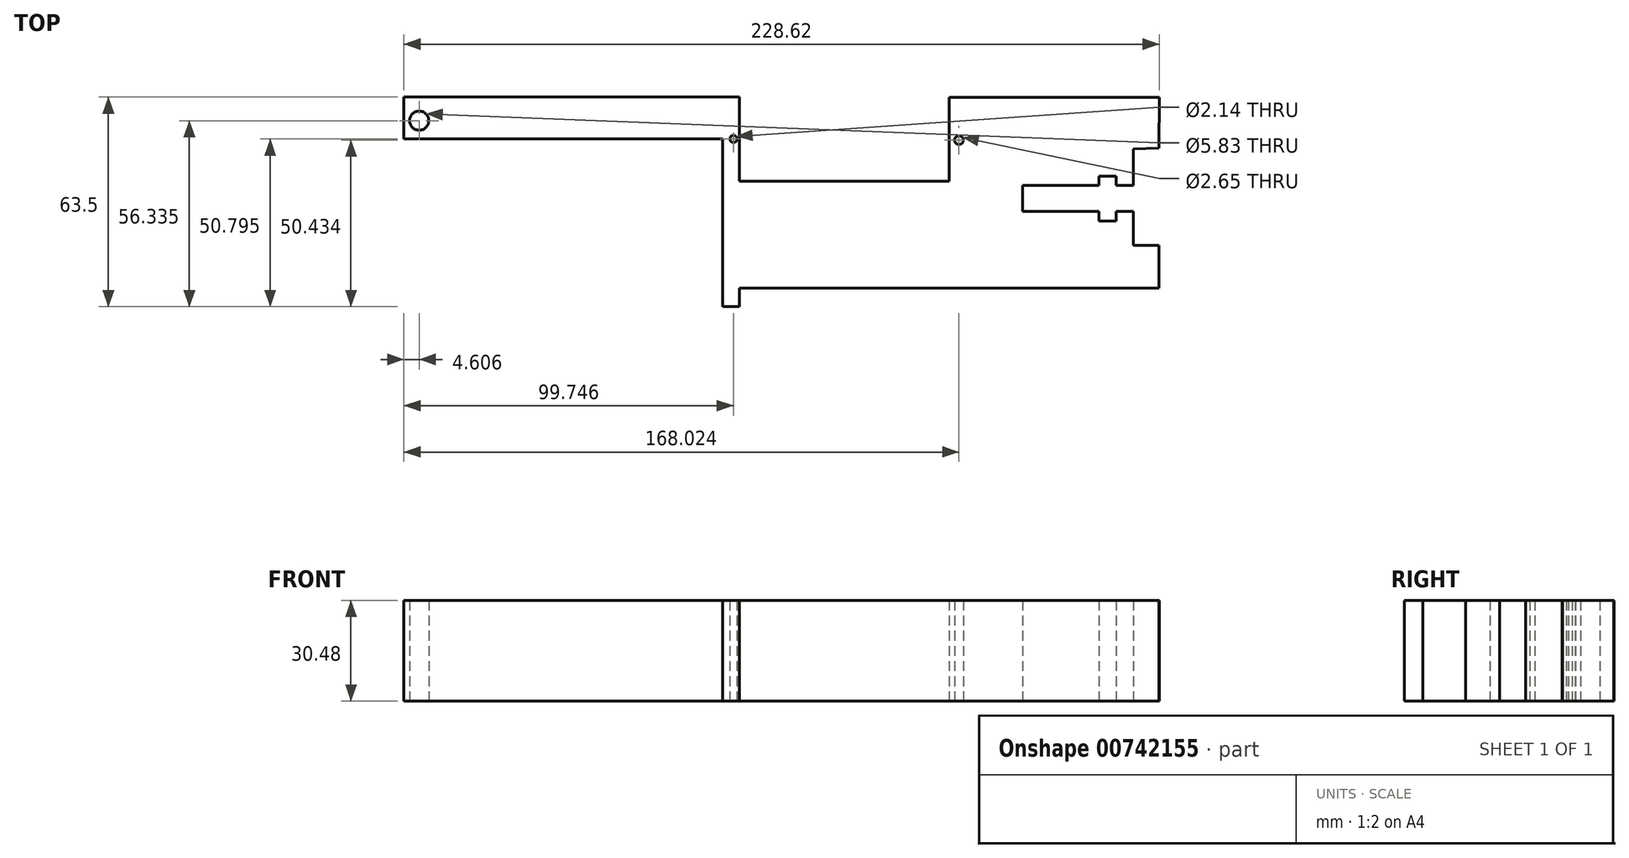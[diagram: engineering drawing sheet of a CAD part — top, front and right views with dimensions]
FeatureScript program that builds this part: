
annotation { "Feature Type Name" : "Feature", "Feature Type Description" : "" }
export const myFeature = defineFeature(function(context is Context, id is Id, definition is map)
    precondition{}
    {
        {
            var Q0;
            Q0=qCreatedBy(makeId("Top.planeOp"),FACE);
            var sketch = newSketch(context, id + "F0", { "sketchPlane" : qUnion([Q0])});
            skLineSegment(sketch, "E0.bottom", {"start": v(-95.7, 37.6) * mm, "end": v(5.9, 37.6) * mm});
            skLineSegment(sketch, "E0.top", {"start": v(-95.7, 24.9) * mm, "end": v(5.9, 24.9) * mm});
            skLineSegment(sketch, "E0.left", {"start": v(-95.7, 37.6) * mm, "end": v(-95.7, 24.9) * mm});
            skLineSegment(sketch, "E0.right", {"start": v(5.9, 37.6) * mm, "end": v(5.9, 24.9) * mm});
            skLineSegment(sketch, "E1.bottom", {"start": v(5.9, 37.6) * mm, "end": v(0.82, 37.6) * mm});
            skLineSegment(sketch, "E1.top", {"start": v(5.9, -25.9) * mm, "end": v(0.82, -25.9) * mm});
            skLineSegment(sketch, "E1.left", {"start": v(5.9, 37.6) * mm, "end": v(5.9, -25.9) * mm});
            skLineSegment(sketch, "E1.right", {"start": v(0.82, 37.6) * mm, "end": v(0.82, -25.9) * mm});
            skLineSegment(sketch, "E2", {"start": v(5.9, -25.9) * mm, "end": v(5.9, -20.3) * mm});
            skLineSegment(sketch, "E3", {"start": v(5.9, -20.3) * mm, "end": v(132.9, -20.3) * mm});
            skLineSegment(sketch, "E4", {"start": v(5.9, 37.6) * mm, "end": v(5.9, 12.14) * mm});
            skLineSegment(sketch, "E5", {"start": v(5.9, 12.14) * mm, "end": v(132.9, 12.14) * mm});
            skLineSegment(sketch, "E6", {"start": v(132.9, 12.14) * mm, "end": v(132.9, -20.3) * mm});
            skLineSegment(sketch, "E7", {"start": v(5.9, 12.14) * mm, "end": v(69.4, 12.14) * mm});
            skLineSegment(sketch, "E8", {"start": v(69.4, 12.14) * mm, "end": v(69.4, 37.47) * mm});
            skLineSegment(sketch, "E9", {"start": v(69.4, 37.47) * mm, "end": v(132.92, 37.47) * mm});
            skLineSegment(sketch, "E10", {"start": v(132.92, 37.47) * mm, "end": v(132.9, 12.14) * mm});
            skLineSegment(sketch, "E11", {"start": v(132.92, 37.47) * mm, "end": v(132.91, 22.06) * mm});
            skLineSegment(sketch, "E12", {"start": v(132.9, -20.3) * mm, "end": v(132.9, -7.37) * mm});
            skLineSegment(sketch, "E13", {"start": v(132.9, -7.37) * mm, "end": v(125.05, -7.37) * mm});
            skLineSegment(sketch, "E14", {"start": v(125.05, -7.37) * mm, "end": v(125.05, 21.9) * mm});
            skLineSegment(sketch, "E15", {"start": v(125.05, 21.9) * mm, "end": v(132.91, 22.06) * mm});
            skLineSegment(sketch, "E16", {"start": v(125.05, -7.37) * mm, "end": v(125.05, 2.9) * mm});
            skLineSegment(sketch, "E17", {"start": v(125.05, 21.9) * mm, "end": v(125.05, 10.77) * mm});
            skLineSegment(sketch, "E18", {"start": v(125.05, 2.9) * mm, "end": v(91.6, 2.9) * mm});
            skLineSegment(sketch, "E19", {"start": v(125.05, 10.77) * mm, "end": v(91.6, 10.77) * mm});
            skLineSegment(sketch, "E20", {"start": v(91.6, 10.77) * mm, "end": v(91.6, 2.9) * mm});
            skLineSegment(sketch, "E21", {"start": v(125.05, 10.77) * mm, "end": v(119.88, 10.77) * mm});
            skLineSegment(sketch, "E22", {"start": v(125.05, 2.9) * mm, "end": v(119.88, 2.9) * mm});
            skLineSegment(sketch, "E23", {"start": v(119.88, 2.9) * mm, "end": v(119.88, 0) * mm});
            skLineSegment(sketch, "E24", {"start": v(119.88, 10.77) * mm, "end": v(119.88, 13.68) * mm});
            skLineSegment(sketch, "E25", {"start": v(119.88, 0) * mm, "end": v(114.66, 0) * mm});
            skLineSegment(sketch, "E26", {"start": v(114.66, 0) * mm, "end": v(114.66, 2.9) * mm});
            skLineSegment(sketch, "E27", {"start": v(114.66, 2.9) * mm, "end": v(119.88, 2.9) * mm});
            skLineSegment(sketch, "E28", {"start": v(119.88, 13.68) * mm, "end": v(114.66, 13.68) * mm});
            skLineSegment(sketch, "E29", {"start": v(114.66, 13.68) * mm, "end": v(114.66, 10.77) * mm});
            skLineSegment(sketch, "E30", {"start": v(114.66, 10.77) * mm, "end": v(119.88, 10.77) * mm});
            skPoint(sketch, "E31.centerSnap0", {"position": v(132.91, 24.8) * mm});
            skCircle(sketch, "E32", {"center": v(4.05, 24.9) * mm, "radius": 1.07 * mm});
            skCircle(sketch, "E33", {"center": v(72.32, 24.53) * mm, "radius": 1.33 * mm});
            skCircle(sketch, "E34", {"center": v(-91.1, 30.44) * mm, "radius": 2.91 * mm});
            skSolve(sketch);
        }
        {
            var Q0;
            {var subQ5=sQuery(id+"F0.wireOp",EDGE,"E0.left");Q0=makeQuery(id+"F0.imprint","IMPRINT",FACE,{"disambiguationData":[TD([[makeQuery(id+"F0.imprint","IMPRINT",EDGE,{"derivedFrom":subQ5}),1.0]])]});}
            var Q1;
            {var subQ0=sQuery(id+"F0.wireOp",EDGE,"E0.right");Q1=makeQuery(id+"F0.imprint","IMPRINT",FACE,{"disambiguationData":[TD([[makeQuery(id+"F0.imprint","IMPRINT",EDGE,{"derivedFrom":subQ0}),-1.0]])]});}
            var Q2;
            {var subQ7=sQuery(id+"F0.wireOp",EDGE,"E1.top");Q2=makeQuery(id+"F0.imprint","IMPRINT",FACE,{"disambiguationData":[TD([[makeQuery(id+"F0.imprint","IMPRINT",EDGE,{"derivedFrom":subQ7}),-1.0]])]});}
            var Q3;
            {var subQ12=sQuery(id+"F0.wireOp",EDGE,"E3");Q3=makeQuery(id+"F0.imprint","IMPRINT",FACE,{"disambiguationData":[TD([[makeQuery(id+"F0.imprint","IMPRINT",EDGE,{"derivedFrom":subQ12}),1.0]])]});}
            var Q4;
            {var subQ9=sQuery(id+"F0.wireOp",EDGE,"E8");Q4=makeQuery(id+"F0.imprint","IMPRINT",FACE,{"disambiguationData":[TD([[makeQuery(id+"F0.imprint","IMPRINT",EDGE,{"derivedFrom":subQ9}),-1.0]])]});}
            var Q5;
            {var subQ0=sQuery(id+"F0.wireOp",EDGE,"E14");var subQ1=sQuery(id+"F0.wireOp",EDGE,"E5");var subQ2=makeQuery(id+"F0.imprint","INTERSECT",VERTEX,{"derivedFrom":[subQ1,subQ0]});Q5=makeQuery(id+"F0.imprint","IMPRINT",FACE,{"disambiguationData":[TD([[makeQuery(id+"F0.imprint","IMPRINT",EDGE,{"disambiguationData":[TD([[subQ2,1.0]])],"derivedFrom":subQ1}),-1.0]])]});}
            extrude(context, id + "F1", {"entities" : qUnion([Q0, Q1, Q2, Q3, Q4, Q5]), "depth" : 5.08 * mm, "offsetDistance" : 25.4 * mm});
        }
        {
            var Q0;
            Q0=makeQuery(id+"F1.opExtrude","CAP_FACE",FACE,{"disambiguationData":[OSD([sQuery(id+"F0.wireOp",EDGE,"E0.bottom"),sQuery(id+"F0.wireOp",EDGE,"E0.top"),sQuery(id+"F0.wireOp",EDGE,"E0.left"),sQuery(id+"F0.wireOp",EDGE,"E0.right"),sQuery(id+"F0.wireOp",EDGE,"E1.top"),sQuery(id+"F0.wireOp",EDGE,"E1.left"),sQuery(id+"F0.wireOp",EDGE,"E1.right"),sQuery(id+"F0.wireOp",EDGE,"E3"),sQuery(id+"F0.wireOp",EDGE,"E5"),sQuery(id+"F0.wireOp",EDGE,"E6"),sQuery(id+"F0.wireOp",EDGE,"E8"),sQuery(id+"F0.wireOp",EDGE,"E9"),sQuery(id+"F0.wireOp",EDGE,"E10"),sQuery(id+"F0.wireOp",EDGE,"E13"),sQuery(id+"F0.wireOp",EDGE,"E14"),sQuery(id+"F0.wireOp",EDGE,"E15"),sQuery(id+"F0.wireOp",EDGE,"E18"),sQuery(id+"F0.wireOp",EDGE,"E19"),sQuery(id+"F0.wireOp",EDGE,"E20"),sQuery(id+"F0.wireOp",EDGE,"E23"),sQuery(id+"F0.wireOp",EDGE,"E24"),sQuery(id+"F0.wireOp",EDGE,"E25"),sQuery(id+"F0.wireOp",EDGE,"E26"),sQuery(id+"F0.wireOp",EDGE,"E28"),sQuery(id+"F0.wireOp",EDGE,"E29"),sQuery(id+"F0.wireOp",EDGE,"E32"),sQuery(id+"F0.wireOp",EDGE,"E33"),sQuery(id+"F0.wireOp",EDGE,"E34")])],"isStart":false});
            extrude(context, id + "F2", {"entities" : qUnion([Q0]), "operationType" : NewBodyOperationType.ADD, "depth" : 25.4 * mm, "offsetDistance" : 25.4 * mm});
        }
    });
